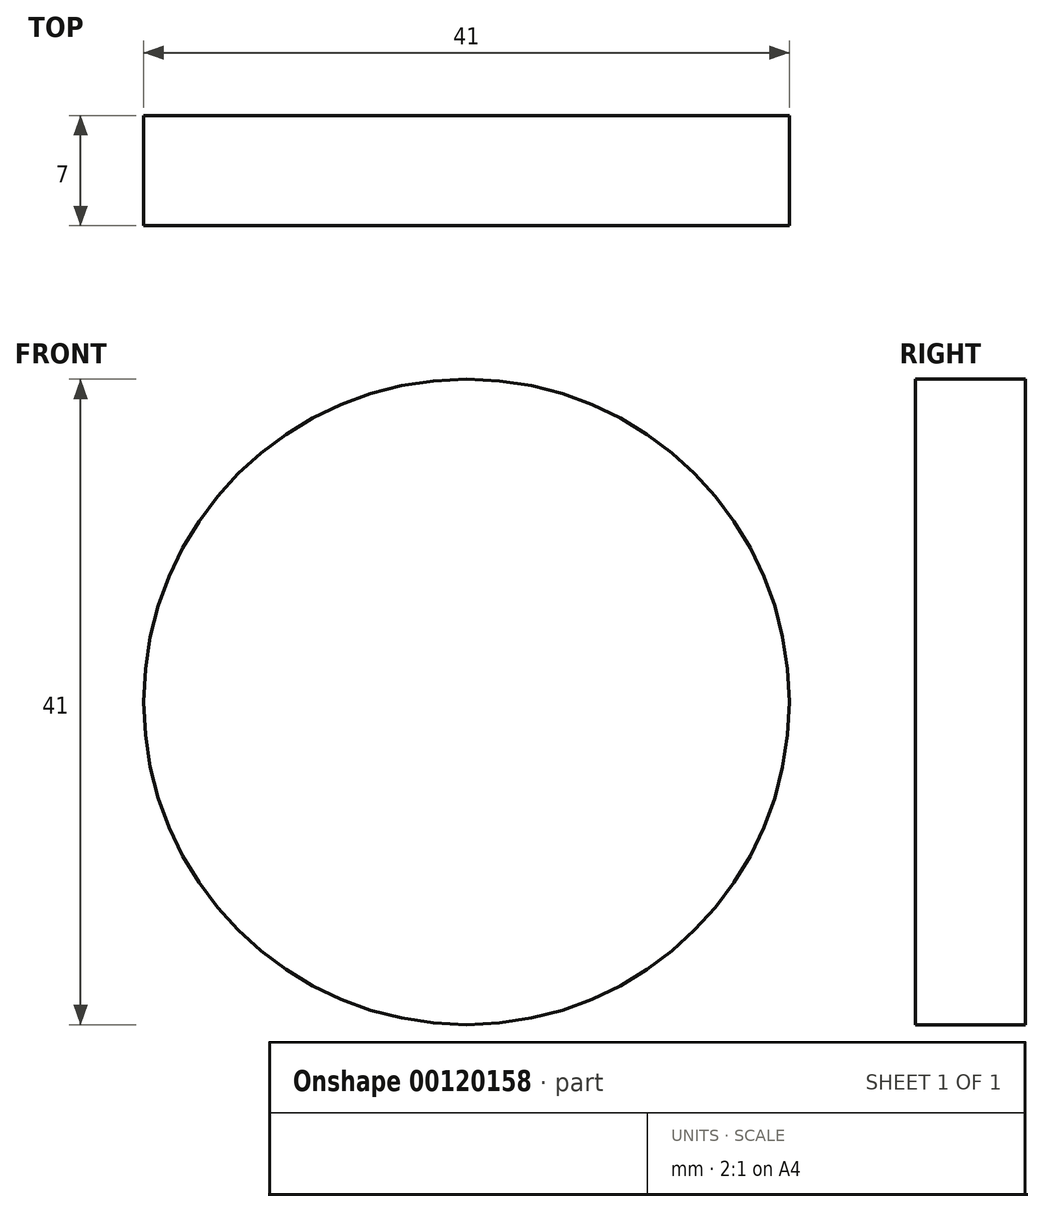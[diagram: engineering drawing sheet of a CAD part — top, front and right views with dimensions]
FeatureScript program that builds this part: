
annotation { "Feature Type Name" : "Feature", "Feature Type Description" : "" }
export const myFeature = defineFeature(function(context is Context, id is Id, definition is map)
    precondition{}
    {
        {
            var Q0;
            Q0=qCreatedBy(makeId("Front.planeOp"),FACE);
            var sketch = newSketch(context, id + "F0", { "sketchPlane" : qUnion([Q0])});
            skCircle(sketch, "E0", {"center": v(0, 0) * mm, "radius": 20.5 * mm});
            skSolve(sketch);
        }
        {
            var Q0;
            Q0 = qSketchRegion(id + "F0", true);
            extrude(context, id + "F1", {"entities" : qUnion([Q0]), "depth" : 7 * mm});
        }
    });
